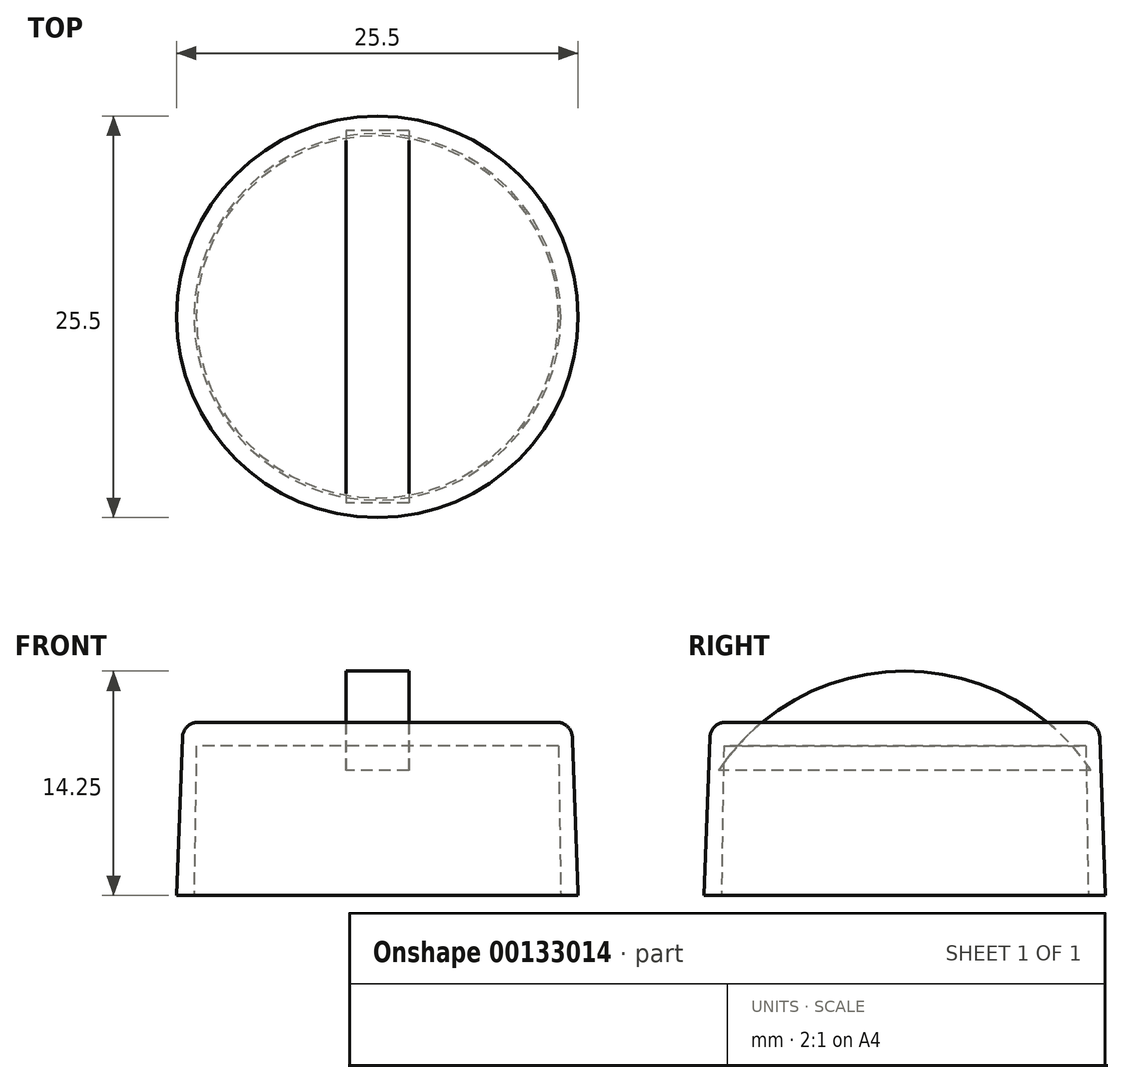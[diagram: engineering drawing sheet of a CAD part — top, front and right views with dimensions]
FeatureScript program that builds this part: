
annotation { "Feature Type Name" : "Feature", "Feature Type Description" : "" }
export const myFeature = defineFeature(function(context is Context, id is Id, definition is map)
    precondition{}
    {
        {
            var Q0;
            Q0=qCreatedBy(makeId("Top.planeOp"),FACE);
            var sketch = newSketch(context, id + "F0", { "sketchPlane" : qUnion([Q0])});
            skCircle(sketch, "E0", {"center": v(0, 0) * mm, "radius": 11.65 * mm});
            skSolve(sketch);
        }
        {
            var Q0;
            Q0=qCreatedBy(makeId("Top.planeOp"),FACE);
            cPlane(context, id + "F1", {"entities" : qUnion([Q0]), "cplaneType" : CPlaneType.OFFSET, "offset" : 9.5 * mm, "width" : 150 * mm, "height" : 150 * mm});
        }
        {
            var Q0;
            Q0=qCreatedBy(id+"F1.planeOp",FACE);
            var sketch = newSketch(context, id + "F2", { "sketchPlane" : qUnion([Q0])});
            skCircle(sketch, "E1", {"center": v(0, 0) * mm, "radius": 11.5 * mm});
            skSolve(sketch);
        }
        {
            var Q0;
            Q0 = qSketchRegion(id + "F0", true);
            var Q1;
            Q1 = qSketchRegion(id + "F2", true);
            loft(context, id + "F3", {"sheetProfilesArray" : [{ "sheetProfileEntities" : qUnion([Q0]) }, { "sheetProfileEntities" : qUnion([Q1]) }]});
        }
        {
            var Q0;
            Q0=qCreatedBy(makeId("Top.planeOp"),FACE);
            var sketch = newSketch(context, id + "F4", { "sketchPlane" : qUnion([Q0])});
            skCircle(sketch, "E2", {"center": v(0, 0) * mm, "radius": 12.75 * mm});
            skSolve(sketch);
        }
        {
            var Q0;
            Q0=qCreatedBy(makeId("Top.planeOp"),FACE);
            cPlane(context, id + "F5", {"entities" : qUnion([Q0]), "cplaneType" : CPlaneType.OFFSET, "offset" : 11 * mm, "width" : 150 * mm, "height" : 150 * mm});
        }
        {
            var Q0;
            Q0=qCreatedBy(id+"F5.planeOp",FACE);
            var sketch = newSketch(context, id + "F6", { "sketchPlane" : qUnion([Q0])});
            skCircle(sketch, "E3", {"center": v(0, 0) * mm, "radius": 12.35 * mm});
            skSolve(sketch);
        }
        {
            var Q1;
            Q1 = qSketchRegion(id + "F6", true);
            var Q2;
            Q2 = qSketchRegion(id + "F4", true);
            loft(context, id + "F7", {"sheetProfilesArray" : [{ "sheetProfileEntities" : qUnion([Q1]) }, { "sheetProfileEntities" : qUnion([Q2]) }]});
        }
        {
            var Q0;
            Q0=makeQuery(id+"F7.opLoft","MID_CAP_EDGE",EDGE,{"disambiguationData":[OSD([sQuery(id+"F6.wireOp",EDGE,"E3")])],"capPos":0.0});
            fillet(context, id + "F8", {"entities" : qUnion([Q0]), "radius" : 1 * mm, "tangentPropagation" : true, "allowEdgeOverflow" : false});
        }
        {
            var Q0;
            Q0=qCreatedBy(makeId("Right.planeOp"),FACE);
            var sketch = newSketch(context, id + "F9", { "sketchPlane" : qUnion([Q0])});
            skCircle(sketch, "E4", {"center": v(0, 0) * mm, "radius": 14.25 * mm});
            skSolve(sketch);
        }
        {
            var Q0;
            Q0=makeQuery(id+"F9.imprint","IMPRINT",FACE,{"disambiguationData":[TD([[makeQuery(id+"F9.imprint","IMPRINT",EDGE,{"derivedFrom":sQuery(id+"F9.wireOp",EDGE,"E4")}),1.0]])]});
            extrude(context, id + "F10", {"entities" : qUnion([Q0]), "endBound" : BoundingType.SYMMETRIC, "depth" : 4 * mm});
        }
        {
            var Q0;
            Q0=qCreatedBy(makeId("Right.planeOp"),FACE);
            var sketch = newSketch(context, id + "F11", { "sketchPlane" : qUnion([Q0])});
            skLineSegment(sketch, "E5.bottom", {"start": v(-14.38, 7.94) * mm, "end": v(14.6, 7.94) * mm});
            skLineSegment(sketch, "E5.top", {"start": v(-14.38, -14.86) * mm, "end": v(14.6, -14.86) * mm});
            skLineSegment(sketch, "E5.left", {"start": v(-14.38, 7.94) * mm, "end": v(-14.38, -14.86) * mm});
            skLineSegment(sketch, "E5.right", {"start": v(14.6, 7.94) * mm, "end": v(14.6, -14.86) * mm});
            skSolve(sketch);
        }
        {
            var Q0;
            Q0=makeQuery(id+"F11.imprint","IMPRINT",FACE,{"disambiguationData":[TD([[makeQuery(id+"F11.imprint","IMPRINT",EDGE,{"derivedFrom":sQuery(id+"F11.wireOp",EDGE,"E5.bottom")}),-1.0]])]});
            extrude(context, id + "F12", {"entities" : qUnion([Q0]), "endBound" : BoundingType.SYMMETRIC, "depth" : 25 * mm});
        }
        {
            var Q0;
            Q0=makeQuery(id+"F12.opExtrude","SWEPT_BODY",BODY,{"disambiguationData":[OSD([sQuery(id+"F11.wireOp",EDGE,"E5.bottom"),sQuery(id+"F11.wireOp",EDGE,"E5.top"),sQuery(id+"F11.wireOp",EDGE,"E5.left"),sQuery(id+"F11.wireOp",EDGE,"E5.right")])]});
            var Q1;
            Q1=makeQuery(id+"F10.opExtrude","SWEPT_BODY",BODY,{"disambiguationData":[OSD([sQuery(id+"F9.wireOp",EDGE,"E4")])]});
            booleanBodies(context, id + "F13", {"operationType" : BooleanOperationType.SUBTRACTION, "tools" : qUnion([Q0]), "targets" : qUnion([Q1])});
        }
        {
            var Q0;
            Q0=makeQuery(id+"F3.opLoft","SWEPT_BODY",BODY,{"disambiguationData":[OSD([makeQuery(id+"F0.imprint","IMPRINT",FACE,{"disambiguationData":[TD([[makeQuery(id+"F0.imprint","IMPRINT",EDGE,{"derivedFrom":sQuery(id+"F0.wireOp",EDGE,"E0")}),1.0]])]}),makeQuery(id+"F2.imprint","IMPRINT",FACE,{"disambiguationData":[TD([[makeQuery(id+"F2.imprint","IMPRINT",EDGE,{"derivedFrom":sQuery(id+"F2.wireOp",EDGE,"E1")}),1.0]])]})])]});
            var Q1;
            Q1=makeQuery(id+"F7.opLoft","SWEPT_BODY",BODY,{"disambiguationData":[OSD([makeQuery(id+"F4.imprint","IMPRINT",FACE,{"disambiguationData":[TD([[makeQuery(id+"F4.imprint","IMPRINT",EDGE,{"derivedFrom":sQuery(id+"F4.wireOp",EDGE,"E2")}),1.0]])]}),makeQuery(id+"F6.imprint","IMPRINT",FACE,{"disambiguationData":[TD([[makeQuery(id+"F6.imprint","IMPRINT",EDGE,{"derivedFrom":sQuery(id+"F6.wireOp",EDGE,"E3")}),1.0]])]})])]});
            booleanBodies(context, id + "F14", {"operationType" : BooleanOperationType.SUBTRACTION, "tools" : qUnion([Q0]), "targets" : qUnion([Q1])});
        }
    });
